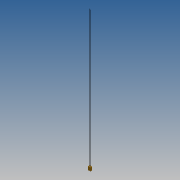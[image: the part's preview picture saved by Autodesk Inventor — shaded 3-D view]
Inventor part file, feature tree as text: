
AUTODESK INVENTOR PART (.ipt)
format: ipt  version: 2014 SP1 (Build 180222100, 222)  size: 133,632 bytes
history: native  units: in
note: dims shown in document units (in); Inventor stores cm internally (conversion verified against a paired STEP export)
features: sketch x8, extrude x4, other x4
ambient origin geometry x8: Origin, YZ Plane, XZ Plane, XY Plane, X Axis, Y Axis, Z Axis, Center Point
bodies: Solid1 (feature_tree)
feature tree (16):
  extrude  "Extrusion1"  Depth=0.1in
  extrude  "Extrusion2"  Depth=1.0in
  extrude  "Extrusion3"  Depth=0.2in
  extrude  "Extrusion4"  Depth=160.0in TaperAngle=0.0deg
  sketch  "Sketch5"  dims[d15=0.5in]
  other  "Pol1_1"
  sketch  "Sketch6"  dims[d16=0.5in]
  other  "Pol1_2"
  sketch  "Sketch7"  dims[d17=1.0in]
  other  "Pol2_1"
  sketch  "Sketch8"  dims[d18=0.4in d19=0.4in d20=0.5in d21=0.0in]
  other  "Pol2_2"
  sketch  "Sketch1"  dims[d0=0.75in d2=0.1in]
  sketch  "Sketch2"  dims[d3=4.0in d4=0.0in d7=1.0in]
  sketch  "Sketch3"  dims[d8=4.0in d9=0.0in d11=0.2in]
  sketch  "Sketch4"  dims[d12=0.2in d13=160.0in d14=0.0in]
